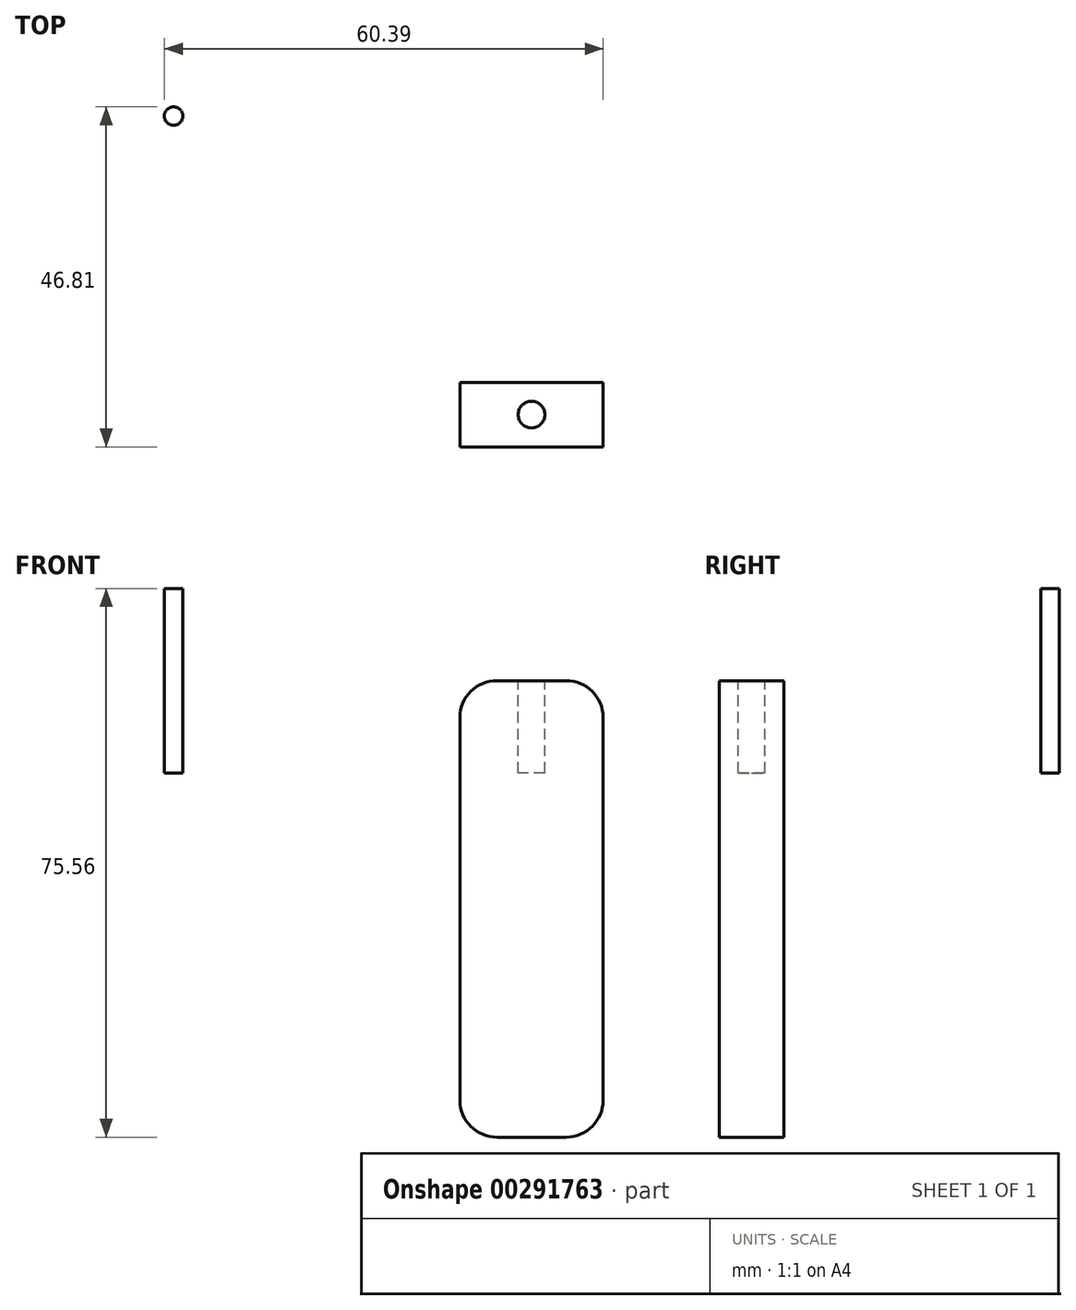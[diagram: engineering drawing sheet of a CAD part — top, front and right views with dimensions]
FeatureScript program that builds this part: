
annotation { "Feature Type Name" : "Feature", "Feature Type Description" : "" }
export const myFeature = defineFeature(function(context is Context, id is Id, definition is map)
    precondition{}
    {
        {
            var Q0;
            Q0=qCreatedBy(makeId("Front.planeOp"),FACE);
            var sketch = newSketch(context, id + "F0", { "sketchPlane" : qUnion([Q0])});
            skLineSegment(sketch, "E0.bottom", {"start": v(-8.67, 23.25) * mm, "end": v(11.04, 23.25) * mm});
            skLineSegment(sketch, "E0.top", {"start": v(-8.67, -39.61) * mm, "end": v(11.04, -39.61) * mm});
            skLineSegment(sketch, "E0.left", {"start": v(-8.67, 23.25) * mm, "end": v(-8.67, -39.61) * mm});
            skLineSegment(sketch, "E0.right", {"start": v(11.04, 23.25) * mm, "end": v(11.04, -39.61) * mm});
            skSolve(sketch);
        }
        {
            var Q0;
            Q0=makeQuery(id+"F0.imprint","IMPRINT",FACE,{"disambiguationData":[TD([[makeQuery(id+"F0.imprint","IMPRINT",EDGE,{"derivedFrom":sQuery(id+"F0.wireOp",EDGE,"E0.bottom")}),-1.0]])]});
            extrude(context, id + "F1", {"entities" : qUnion([Q0]), "depth" : 8.9 * mm});
        }
        {
            var Q0;
            Q0=makeQuery(id+"F1.opExtrude","SWEPT_EDGE",EDGE,{"disambiguationData":[OSD([sQuery(id+"F0.wireOp",EDGE,"E0.top"),sQuery(id+"F0.wireOp",EDGE,"E0.left")])]});
            var Q1;
            Q1=makeQuery(id+"F1.opExtrude","SWEPT_EDGE",EDGE,{"disambiguationData":[OSD([sQuery(id+"F0.wireOp",EDGE,"E0.top"),sQuery(id+"F0.wireOp",EDGE,"E0.right")])]});
            var Q2;
            Q2=makeQuery(id+"F1.opExtrude","SWEPT_EDGE",EDGE,{"disambiguationData":[OSD([sQuery(id+"F0.wireOp",EDGE,"E0.bottom"),sQuery(id+"F0.wireOp",EDGE,"E0.right")])]});
            var Q3;
            Q3=makeQuery(id+"F1.opExtrude","SWEPT_EDGE",EDGE,{"disambiguationData":[OSD([sQuery(id+"F0.wireOp",EDGE,"E0.bottom"),sQuery(id+"F0.wireOp",EDGE,"E0.left")])]});
            fillet(context, id + "F2", {"entities" : qUnion([Q0, Q1, Q2, Q3]), "radius" : 5.08 * mm, "tangentPropagation" : true, "allowEdgeOverflow" : false});
        }
        {
            var Q0;
            Q0=makeQuery(id+"F1.opExtrude","SWEPT_FACE",FACE,{"disambiguationData":[OSD([sQuery(id+"F0.wireOp",EDGE,"E0.bottom")])]});
            var sketch = newSketch(context, id + "F3", { "sketchPlane" : qUnion([Q0])});
            skCircle(sketch, "E1", {"center": v(1.18, -4.45) * mm, "radius": 1.84 * mm});
            skPoint(sketch, "E1.centerSnap0", {"position": v(5.96, -4.45) * mm});
            skPoint(sketch, "E1.centerSnap1", {"position": v(1.18, 0) * mm});
            skSolve(sketch);
        }
        {
            var Q0;
            Q0 = qSketchRegion(id + "F3", true);
            extrude(context, id + "F4", {"entities" : qUnion([Q0]), "operationType" : NewBodyOperationType.REMOVE, "oppositeDirection" : true, "depth" : 12.7 * mm});
        }
        {
            var Q0;
            Q0=makeQuery(id+"F4.boolean.opBoolean","COPY",FACE,{"derivedFrom":makeQuery(id+"F4.opExtrude","CAP_FACE",FACE,{"disambiguationData":[OSD([sQuery(id+"F3.wireOp",EDGE,"E1")])],"isStart":false})});
            var sketch = newSketch(context, id + "F5", { "sketchPlane" : qUnion([Q0])});
            skCircle(sketch, "E2", {"center": v(-48.08, 36.65) * mm, "radius": 1.27 * mm});
            skSolve(sketch);
        }
        {
            var Q0;
            Q0=makeQuery(id+"F5.imprint","IMPRINT",FACE,{"disambiguationData":[TD([[makeQuery(id+"F5.imprint","IMPRINT",EDGE,{"derivedFrom":sQuery(id+"F5.wireOp",EDGE,"E2")}),1.0]])]});
            extrude(context, id + "F6", {"entities" : qUnion([Q0]), "depth" : 25.4 * mm});
        }
    });
